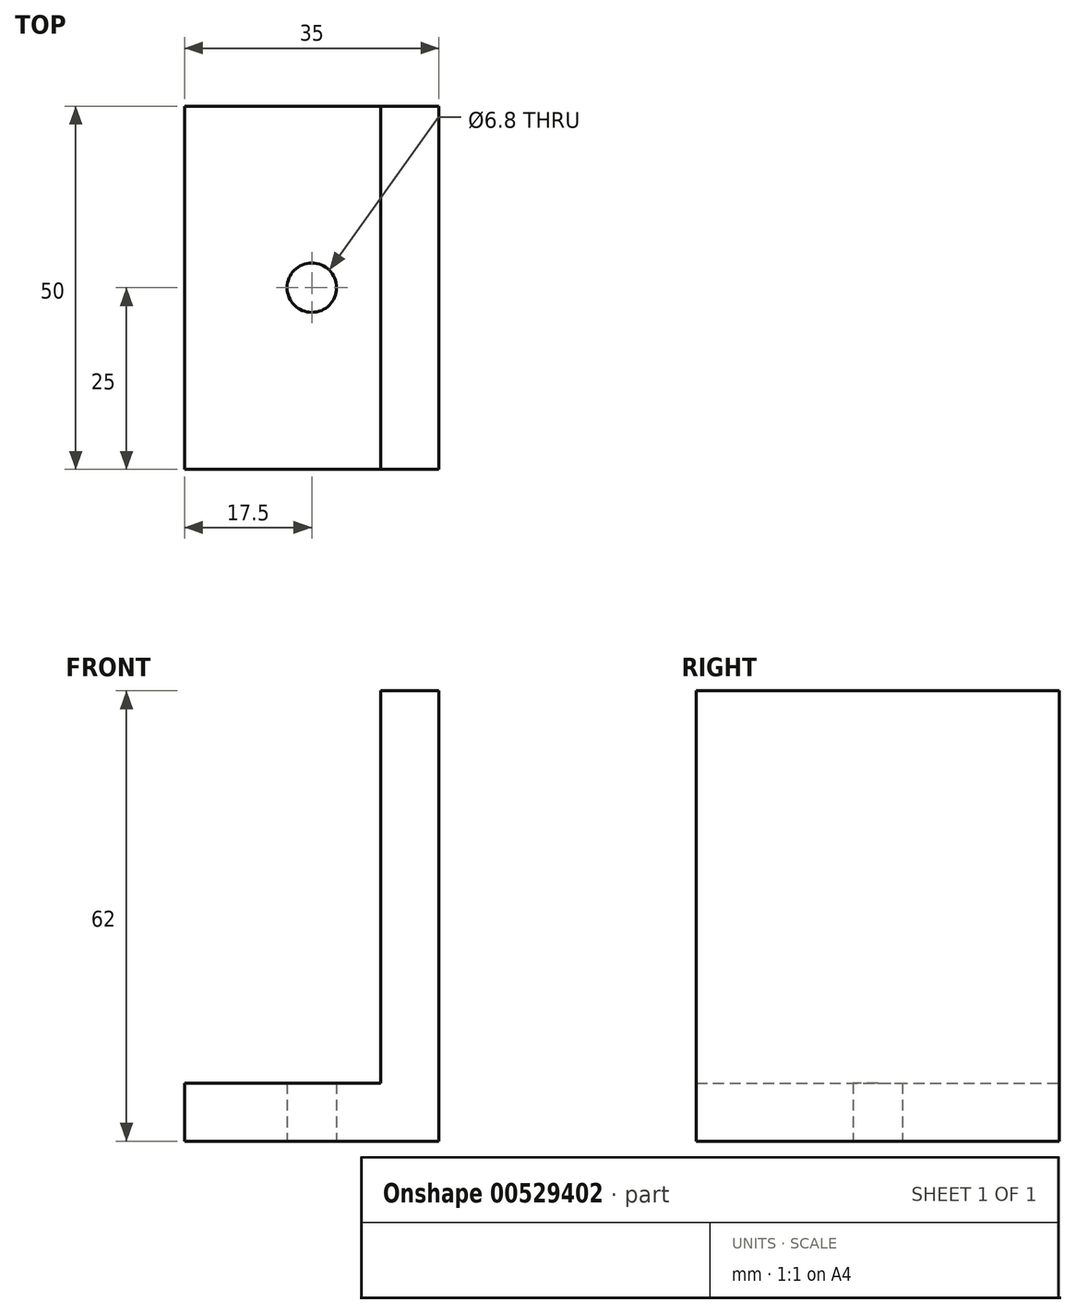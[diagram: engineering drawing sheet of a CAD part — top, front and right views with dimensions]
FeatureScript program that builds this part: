
annotation { "Feature Type Name" : "Feature", "Feature Type Description" : "" }
export const myFeature = defineFeature(function(context is Context, id is Id, definition is map)
    precondition{}
    {
        {
            var Q0;
            Q0=qCreatedBy(makeId("Front.planeOp"),FACE);
            var sketch = newSketch(context, id + "F0", { "sketchPlane" : qUnion([Q0])});
            skLineSegment(sketch, "E0.bottom", {"start": v(-7.8, 1.1) * mm, "end": v(19.2, 1.1) * mm});
            skLineSegment(sketch, "E0.top", {"start": v(-7.8, -6.9) * mm, "end": v(19.2, -6.9) * mm});
            skLineSegment(sketch, "E0.left", {"start": v(-7.8, 1.1) * mm, "end": v(-7.8, -6.9) * mm});
            skLineSegment(sketch, "E0.right", {"start": v(19.2, 1.1) * mm, "end": v(19.2, -6.9) * mm});
            skLineSegment(sketch, "E1.bottom", {"start": v(19.2, -6.9) * mm, "end": v(27.2, -6.9) * mm});
            skLineSegment(sketch, "E1.top", {"start": v(19.2, -6.9) * mm, "end": v(27.2, -6.9) * mm});
            skLineSegment(sketch, "E1.left", {"start": v(19.2, -6.9) * mm, "end": v(19.2, -6.9) * mm});
            skLineSegment(sketch, "E1.right", {"start": v(27.2, -6.9) * mm, "end": v(27.2, -6.9) * mm});
            skLineSegment(sketch, "E2.top", {"start": v(19.2, 55.1) * mm, "end": v(27.2, 55.1) * mm});
            skLineSegment(sketch, "E2.left", {"start": v(19.2, -6.9) * mm, "end": v(19.2, 55.1) * mm});
            skLineSegment(sketch, "E2.right", {"start": v(27.2, -6.9) * mm, "end": v(27.2, 55.1) * mm});
            skSolve(sketch);
        }
        {
            var Q0;
            {var subQ0=sQuery(id+"F0.wireOp",EDGE,"E0.bottom");Q0=makeQuery(id+"F0.imprint","IMPRINT",FACE,{"disambiguationData":[TD([[makeQuery(id+"F0.imprint","IMPRINT",EDGE,{"derivedFrom":subQ0}),-1.0]])]});}
            var Q1;
            {var subQ3=sQuery(id+"F0.wireOp",EDGE,"E1.bottom");Q1=makeQuery(id+"F0.imprint","IMPRINT",FACE,{"disambiguationData":[TD([[makeQuery(id+"F0.imprint","IMPRINT",EDGE,{"derivedFrom":subQ3}),1.0]])]});}
            extrude(context, id + "F1", {"entities" : qUnion([Q0, Q1]), "depth" : 50 * mm, "offsetDistance" : 25 * mm});
        }
        {
            var Q0;
            Q0=makeQuery(id+"F1.opExtrude","SWEPT_FACE",FACE,{"disambiguationData":[OSD([sQuery(id+"F0.wireOp",EDGE,"E0.top"),sQuery(id+"F0.wireOp",EDGE,"E1.bottom")])]});
            var sketch = newSketch(context, id + "F2", { "sketchPlane" : qUnion([Q0])});
            skLineSegment(sketch, "E3", {"start": v(27.2, 25) * mm, "end": v(-7.8, 25) * mm});
            skLineSegment(sketch, "E4", {"start": v(9.7, 0) * mm, "end": v(9.7, 50) * mm});
            skPoint(sketch, "E5", {"position": v(9.7, 25) * mm});
            skSolve(sketch);
        }
        {
            var Q0;
            Q0=sQuery(id+"F2.wireOp",VERTEX,"E5");
            var Q1;
            Q1=makeQuery(id+"F1.opExtrude","SWEPT_BODY",BODY,{"disambiguationData":[OSD([sQuery(id+"F0.wireOp",EDGE,"E0.bottom"),sQuery(id+"F0.wireOp",EDGE,"E0.top"),sQuery(id+"F0.wireOp",EDGE,"E0.left"),sQuery(id+"F0.wireOp",EDGE,"E1.bottom"),sQuery(id+"F0.wireOp",EDGE,"E2.top"),sQuery(id+"F0.wireOp",EDGE,"E2.left"),sQuery(id+"F0.wireOp",EDGE,"E2.right")])]});
            hole(context, id + "F3", {"style" : HoleStyle.SIMPLE, "endStyle" : HoleEndStyle.THROUGH, "standardTappedOrClearance" : lookupTablePath({ "standard" : "ISO", "engagement" : "75%", "pitch" : "1.25 mm", "size" : "M8", "type" : "Tapped" }), "standardBlindInLast" : lookupTablePath({ "standard" : "ISO", "engagement" : "75%", "pitch" : "1.25 mm", "size" : "M8", "type" : "Tapped" }), "holeDiameter" : 6.8 * mm, "showTappedDepth" : true, "isTappedThrough" : true, "tappedDepth" : 12 * mm, "tapClearance" : 3, "locations" : qUnion([Q0]), "scope" : qUnion([Q1]), "majorDiameter" : 8 * mm});
        }
    });
